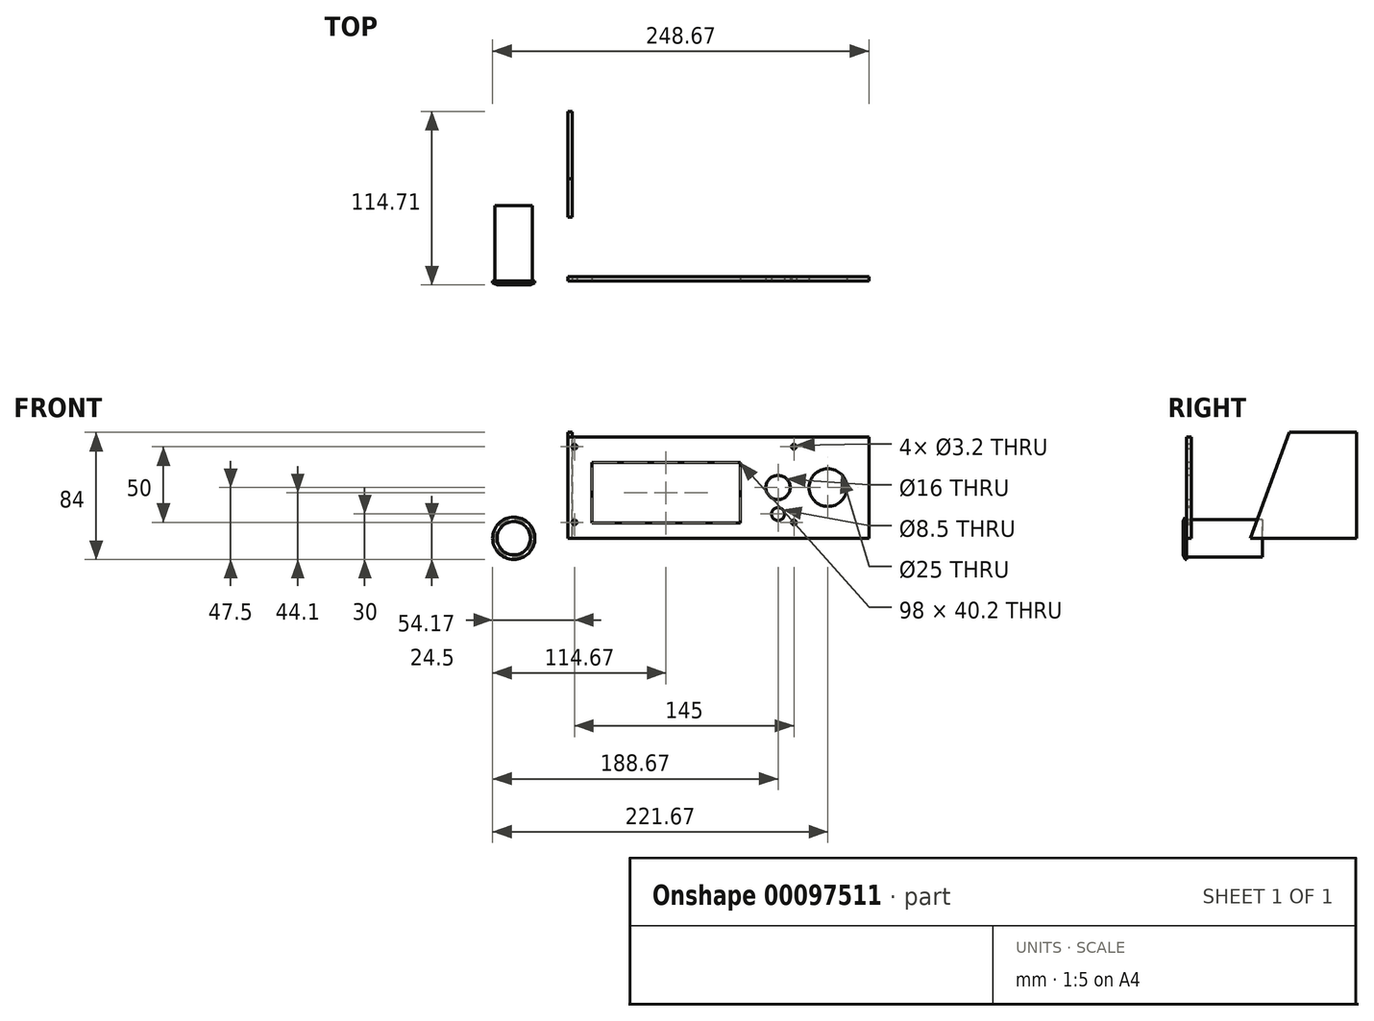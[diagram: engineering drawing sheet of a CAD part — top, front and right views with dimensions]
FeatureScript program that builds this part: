
annotation { "Feature Type Name" : "Feature", "Feature Type Description" : "" }
export const myFeature = defineFeature(function(context is Context, id is Id, definition is map)
    precondition{}
    {
        {
            var Q0;
            Q0=qCreatedBy(makeId("Front.planeOp"),FACE);
            var sketch = newSketch(context, id + "F0", { "sketchPlane" : qUnion([Q0])});
            skLineSegment(sketch, "E0.bottom", {"start": v(0, 0) * mm, "end": v(199, 0) * mm});
            skLineSegment(sketch, "E0.top", {"start": v(0, 67) * mm, "end": v(199, 67) * mm});
            skLineSegment(sketch, "E0.left", {"start": v(0, 0) * mm, "end": v(0, 67) * mm});
            skLineSegment(sketch, "E0.right", {"start": v(199, 0) * mm, "end": v(199, 67) * mm});
            skSolve(sketch);
        }
        {
            var Q0;
            Q0 = qSketchRegion(id + "F0", true);
            extrude(context, id + "F1", {"entities" : qUnion([Q0]), "oppositeDirection" : true, "depth" : 3 * mm});
        }
        {
            var Q0;
            Q0=makeQuery(id+"F1.opExtrude","CAP_FACE",FACE,{"disambiguationData":[OSD([sQuery(id+"F0.wireOp",EDGE,"E0.bottom"),sQuery(id+"F0.wireOp",EDGE,"E0.top"),sQuery(id+"F0.wireOp",EDGE,"E0.left"),sQuery(id+"F0.wireOp",EDGE,"E0.right")])],"isStart":true});
            var sketch = newSketch(context, id + "F2", { "sketchPlane" : qUnion([Q0])});
            skCircle(sketch, "E1", {"center": v(4.5, 10.5) * mm, "radius": 1.6 * mm});
            skCircle(sketch, "E2.0.1.0", {"center": v(4.5, 60.5) * mm, "radius": 1.6 * mm});
            skCircle(sketch, "E2.1.0.0", {"center": v(149.5, 10.5) * mm, "radius": 1.6 * mm});
            skCircle(sketch, "E2.1.1.0", {"center": v(149.5, 60.5) * mm, "radius": 1.6 * mm});
            skLineSegment(sketch, "E2.direction1", {"start": v(4.5, 10.5) * mm, "end": v(149.5, 10.5) * mm, "construction": true});
            skLineSegment(sketch, "E2.direction2", {"start": v(4.5, 10.5) * mm, "end": v(4.5, 60.5) * mm, "construction": true});
            skSolve(sketch);
        }
        {
            var Q0;
            Q0 = qSketchRegion(id + "F2", true);
            extrude(context, id + "F3", {"entities" : qUnion([Q0]), "operationType" : NewBodyOperationType.REMOVE, "endBound" : BoundingType.THROUGH_ALL, "oppositeDirection" : true, "depth" : 25 * mm});
        }
        {
            var Q0;
            Q0=makeQuery(id+"F1.opExtrude","CAP_FACE",FACE,{"disambiguationData":[OSD([sQuery(id+"F0.wireOp",EDGE,"E0.bottom"),sQuery(id+"F0.wireOp",EDGE,"E0.top"),sQuery(id+"F0.wireOp",EDGE,"E0.left"),sQuery(id+"F0.wireOp",EDGE,"E0.right")])],"isStart":true});
            var sketch = newSketch(context, id + "F4", { "sketchPlane" : qUnion([Q0])});
            skLineSegment(sketch, "E3.bottom", {"start": v(16, 10) * mm, "end": v(114, 10) * mm});
            skLineSegment(sketch, "E3.top", {"start": v(16, 50.2) * mm, "end": v(114, 50.2) * mm});
            skLineSegment(sketch, "E3.left", {"start": v(16, 10) * mm, "end": v(16, 50.2) * mm});
            skLineSegment(sketch, "E3.right", {"start": v(114, 10) * mm, "end": v(114, 50.2) * mm});
            skSolve(sketch);
        }
        {
            var Q0;
            Q0 = qSketchRegion(id + "F4", true);
            extrude(context, id + "F5", {"entities" : qUnion([Q0]), "operationType" : NewBodyOperationType.REMOVE, "endBound" : BoundingType.THROUGH_ALL, "oppositeDirection" : true, "depth" : 25 * mm});
        }
        {
            var Q0;
            Q0=makeQuery(id+"F1.opExtrude","CAP_FACE",FACE,{"disambiguationData":[OSD([sQuery(id+"F0.wireOp",EDGE,"E0.bottom"),sQuery(id+"F0.wireOp",EDGE,"E0.top"),sQuery(id+"F0.wireOp",EDGE,"E0.left"),sQuery(id+"F0.wireOp",EDGE,"E0.right")])],"isStart":true});
            var sketch = newSketch(context, id + "F6", { "sketchPlane" : qUnion([Q0])});
            skCircle(sketch, "E4", {"center": v(139, 16) * mm, "radius": 4.25 * mm});
            skCircle(sketch, "E5", {"center": v(139, 33.5) * mm, "radius": 8 * mm});
            skSolve(sketch);
        }
        {
            var Q0;
            Q0 = qSketchRegion(id + "F6", true);
            extrude(context, id + "F7", {"entities" : qUnion([Q0]), "operationType" : NewBodyOperationType.REMOVE, "endBound" : BoundingType.THROUGH_ALL, "oppositeDirection" : true, "depth" : 25 * mm});
        }
        {
            var Q0;
            Q0=makeQuery(id+"F1.opExtrude","CAP_FACE",FACE,{"disambiguationData":[OSD([sQuery(id+"F0.wireOp",EDGE,"E0.bottom"),sQuery(id+"F0.wireOp",EDGE,"E0.top"),sQuery(id+"F0.wireOp",EDGE,"E0.left"),sQuery(id+"F0.wireOp",EDGE,"E0.right")])],"isStart":true});
            var sketch = newSketch(context, id + "F8", { "sketchPlane" : qUnion([Q0])});
            skCircle(sketch, "E6", {"center": v(172, 33.5) * mm, "radius": 12.5 * mm});
            skSolve(sketch);
        }
        {
            var Q0;
            Q0 = qSketchRegion(id + "F8", true);
            extrude(context, id + "F9", {"entities" : qUnion([Q0]), "operationType" : NewBodyOperationType.REMOVE, "endBound" : BoundingType.THROUGH_ALL, "oppositeDirection" : true, "depth" : 25 * mm});
        }
        {
            var Q0;
            Q0=qCreatedBy(makeId("Front.planeOp"),FACE);
            var sketch = newSketch(context, id + "F10", { "sketchPlane" : qUnion([Q0])});
            skCircle(sketch, "E7", {"center": v(-35.67, 0) * mm, "radius": 12.4 * mm});
            skSolve(sketch);
        }
        {
            var Q0;
            Q0 = qSketchRegion(id + "F10", true);
            extrude(context, id + "F11", {"entities" : qUnion([Q0]), "oppositeDirection" : true, "depth" : 50 * mm});
        }
        {
            var Q0;
            Q0=makeQuery(id+"F11.opExtrude","CAP_FACE",FACE,{"disambiguationData":[OSD([sQuery(id+"F10.wireOp",EDGE,"E7")])],"isStart":true});
            var sketch = newSketch(context, id + "F12", { "sketchPlane" : qUnion([Q0])});
            skCircle(sketch, "E8", {"center": v(-35.67, 0) * mm, "radius": 14 * mm});
            skSolve(sketch);
        }
        {
            var Q0;
            Q0 = qSketchRegion(id + "F12", true);
            extrude(context, id + "F13", {"entities" : qUnion([Q0]), "operationType" : NewBodyOperationType.ADD, "depth" : 2.5 * mm});
        }
        {
            var Q0;
            Q0=makeQuery(id+"F13.opExtrude","CAP_EDGE",EDGE,{"disambiguationData":[OSD([sQuery(id+"F12.wireOp",EDGE,"E8")])],"isStart":false});
            chamfer(context, id + "F14", {"entities" : qUnion([Q0]), "chamferType" : ChamferType.TWO_OFFSETS, "width1" : 3 * mm, "oppositeDirection" : false, "width2" : 1.5 * mm, "tangentPropagation" : true});
        }
        {
            var Q0;
            Q0=qCreatedBy(makeId("Right.planeOp"),FACE);
            var sketch = newSketch(context, id + "F15", { "sketchPlane" : qUnion([Q0])});
            skLineSegment(sketch, "E9", {"start": v(42.2, 0) * mm, "end": v(112.2, 0) * mm});
            skLineSegment(sketch, "E10", {"start": v(112.2, 0) * mm, "end": v(112.2, 70) * mm});
            skLineSegment(sketch, "E11", {"start": v(112.2, 70) * mm, "end": v(67.68, 70) * mm});
            skLineSegment(sketch, "E12", {"start": v(67.68, 70) * mm, "end": v(42.2, 0) * mm});
            skSolve(sketch);
        }
        {
            var Q0;
            Q0 = qSketchRegion(id + "F15", true);
            extrude(context, id + "F16", {"entities" : qUnion([Q0]), "depth" : 3 * mm});
        }
    });
